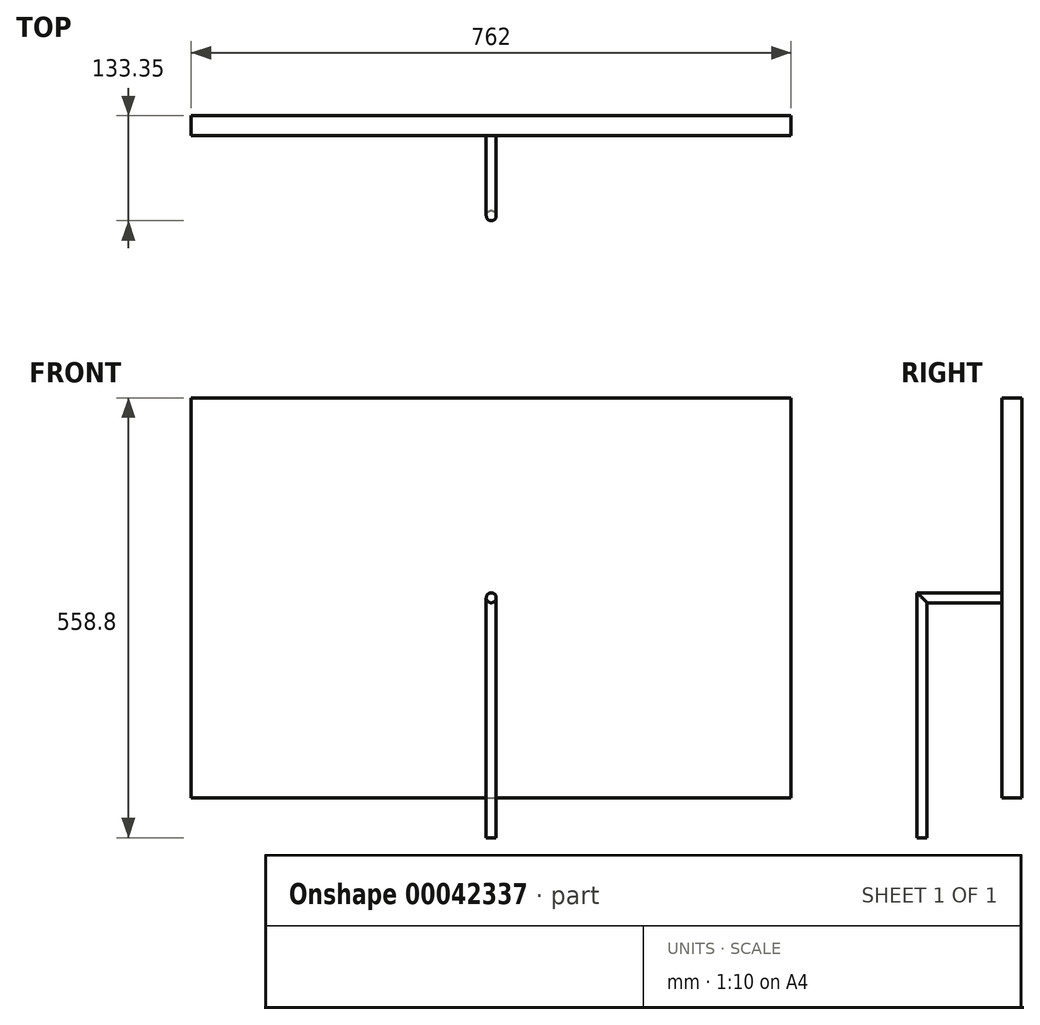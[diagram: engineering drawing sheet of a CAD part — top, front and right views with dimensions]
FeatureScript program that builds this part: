
annotation { "Feature Type Name" : "Feature", "Feature Type Description" : "" }
export const myFeature = defineFeature(function(context is Context, id is Id, definition is map)
    precondition{}
    {
        {
            var Q0;
            Q0=qCreatedBy(makeId("Front.planeOp"),FACE);
            var sketch = newSketch(context, id + "F0", { "sketchPlane" : qUnion([Q0])});
            skLineSegment(sketch, "E0.bottom", {"start": v(-381, 254) * mm, "end": v(381, 254) * mm});
            skLineSegment(sketch, "E0.top", {"start": v(-381, -254) * mm, "end": v(381, -254) * mm});
            skLineSegment(sketch, "E0.left", {"start": v(-381, 254) * mm, "end": v(-381, -254) * mm});
            skLineSegment(sketch, "E0.right", {"start": v(381, 254) * mm, "end": v(381, -254) * mm});
            skSolve(sketch);
        }
        {
            var Q0;
            Q0 = qSketchRegion(id + "F0", true);
            extrude(context, id + "F1", {"entities" : qUnion([Q0]), "depth" : 25.4 * mm});
        }
        {
            var Q0;
            Q0=qCreatedBy(makeId("Right.planeOp"),FACE);
            var sketch = newSketch(context, id + "F2", { "sketchPlane" : qUnion([Q0])});
            skLineSegment(sketch, "E1", {"start": v(0, 0) * mm, "end": v(-127, 0) * mm});
            skLineSegment(sketch, "E2", {"start": v(-127, 0) * mm, "end": v(-127, -304.8) * mm});
            skSolve(sketch);
        }
        {
            var Q0;
            Q0=qCreatedBy(makeId("Front.planeOp"),FACE);
            var sketch = newSketch(context, id + "F3", { "sketchPlane" : qUnion([Q0])});
            skCircle(sketch, "E3", {"center": v(0, 0) * mm, "radius": 6.35 * mm});
            skSolve(sketch);
        }
        {
            var Q0;
            Q0 = qSketchRegion(id + "F3", true);
            var Q1;
            Q1 = qConstructionFilter(qBodyType(qCreatedBy(id + "F2" ,EDGE), BodyType.WIRE), ConstructionObject.NO);
            sweep(context, id + "F4", {"operationType" : NewBodyOperationType.ADD, "profiles" : qUnion([Q0]), "path" : qUnion([Q1])});
        }
    });
